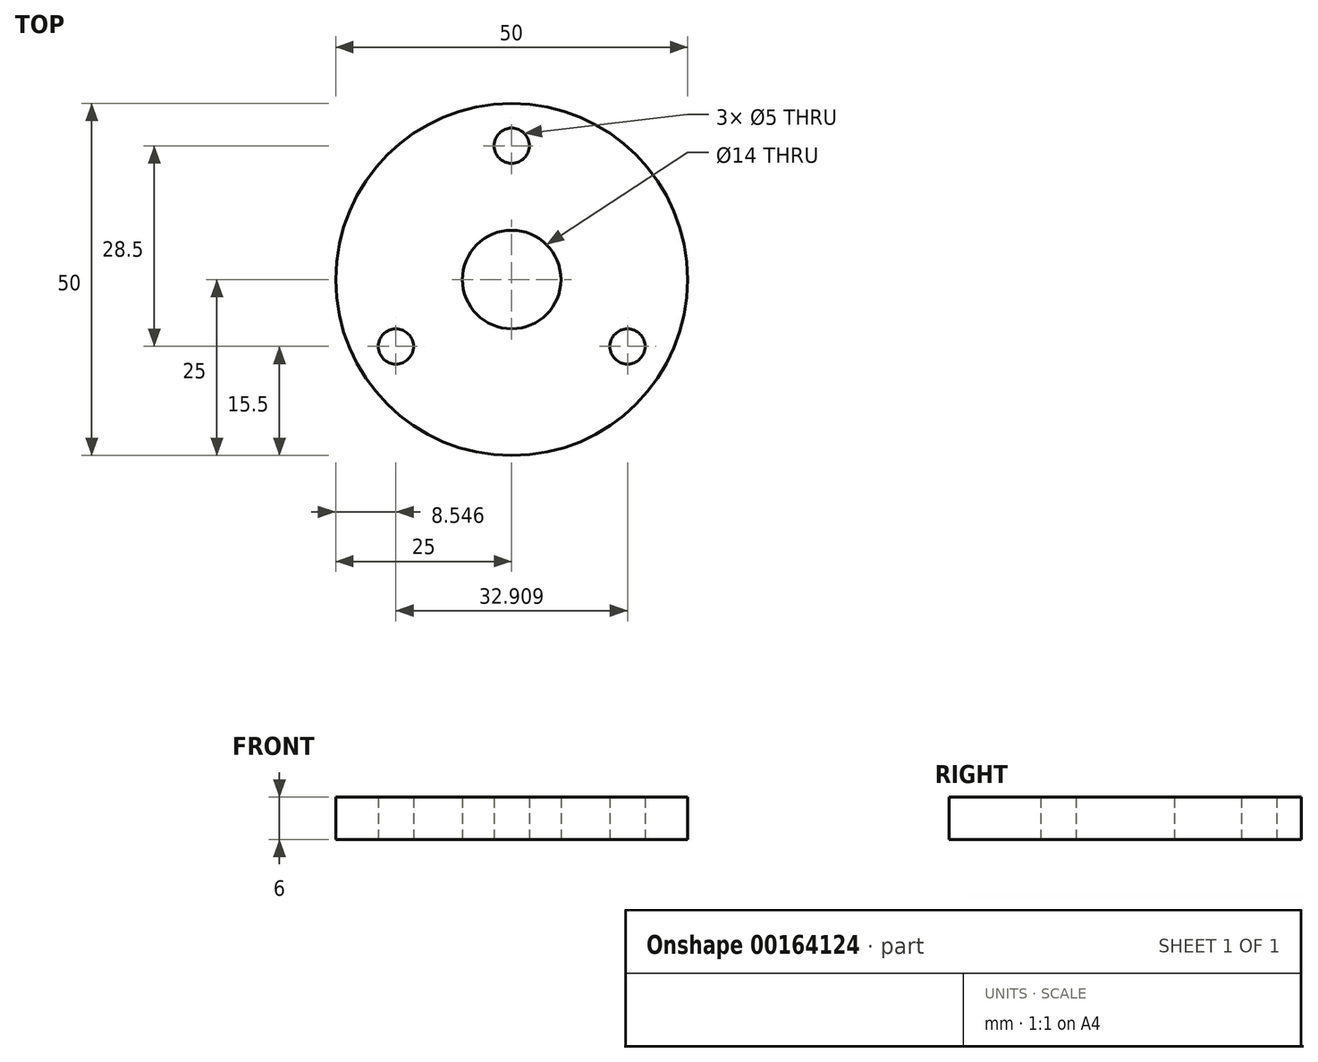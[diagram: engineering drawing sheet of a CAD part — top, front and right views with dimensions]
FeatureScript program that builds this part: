
annotation { "Feature Type Name" : "Feature", "Feature Type Description" : "" }
export const myFeature = defineFeature(function(context is Context, id is Id, definition is map)
    precondition{}
    {
        {
            var Q0;
            Q0=qCreatedBy(makeId("Top.planeOp"),FACE);
            var sketch = newSketch(context, id + "F0", { "sketchPlane" : qUnion([Q0])});
            skCircle(sketch, "E0", {"center": v(0, 0) * mm, "radius": 25 * mm});
            skCircle(sketch, "E1", {"center": v(0, 0) * mm, "radius": 7 * mm});
            skCircle(sketch, "E2", {"center": v(0, 19) * mm, "radius": 2.5 * mm});
            skCircle(sketch, "E3.1.0", {"center": v(-16.45, -9.5) * mm, "radius": 2.5 * mm});
            skCircle(sketch, "E3.2.0", {"center": v(16.45, -9.5) * mm, "radius": 2.5 * mm});
            skSolve(sketch);
        }
        {
            var Q0;
            Q0=makeQuery(id+"F0.imprint","IMPRINT",FACE,{"disambiguationData":[TD([[makeQuery(id+"F0.imprint","IMPRINT",EDGE,{"derivedFrom":sQuery(id+"F0.wireOp",EDGE,"E0")}),1.0]])]});
            extrude(context, id + "F1", {"entities" : qUnion([Q0]), "depth" : 6 * mm});
        }
    });
